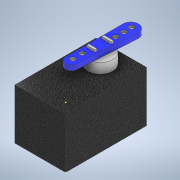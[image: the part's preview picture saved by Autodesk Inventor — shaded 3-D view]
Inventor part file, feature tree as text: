
AUTODESK INVENTOR PART (.ipt)
format: ipt  version: 2021 (Build 250183000, 183)  size: 176,640 bytes
history: native  units: mm
features: sketch x9, extrude x4, hole x3, fillet x2
ambient origin geometry x8: Origin, YZ Plane, XZ Plane, XY Plane, X Axis, Y Axis, Z Axis, Center Point
bodies: Solid1 (feature_tree)
feature tree (18):
  sketch  "Sketch1"  dims[d0=80.0mm d1=50.0mm]
  extrude  "Extrusion1"  Depth=50.0mm
  extrude  "Extrusion2"  Depth=10.0mm TaperAngle=0.0deg
  extrude  "Extrusion3"  Depth=2.0mm TaperAngle=0.0deg
  fillet  "Fillet1"  [1 undecoded]
  fillet  "Fillet2"  [1 undecoded]
  hole  "Hole1"  [1 undecoded]
  hole  "Hole2"  [1 undecoded]
  hole  "Hole3"  [1 undecoded]
  extrude  "Extrusion4"  [1 undecoded]
  sketch  "Sketch9"
  sketch  "Sketch2"  dims[d2=50.0mm d3=0.0mm d4=10.0mm d5=0.0mm]
  sketch  "Sketch3"  dims[d6=5.0mm d7=0.0mm]
  sketch  "Sketch4"  dims[d8=5.0mm d9=6.0mm d10=4.0mm d11=2.0mm d12=90.0deg d13=2.0mm d14=0.0mm]
  sketch  "Sketch5"  dims[d15=5.0mm d16=6.0mm d17=4.0mm d18=2.0mm d19=90.0deg d20=2.0mm d21=0.0mm]
  sketch  "Sketch6"  dims[d22=5.0mm d23=6.0mm d24=4.0mm d25=2.0mm d26=90.0deg d27=2.0mm d28=0.0mm d29=2.0mm d30=0.0mm]
  sketch  "Sketch7"
  sketch  "Sketch8"
note: 6 required parameter values undecoded (feature->parameter linkage not recoverable at this tier; creation-order binding heuristic only, values carry confidence <= 0.55)
